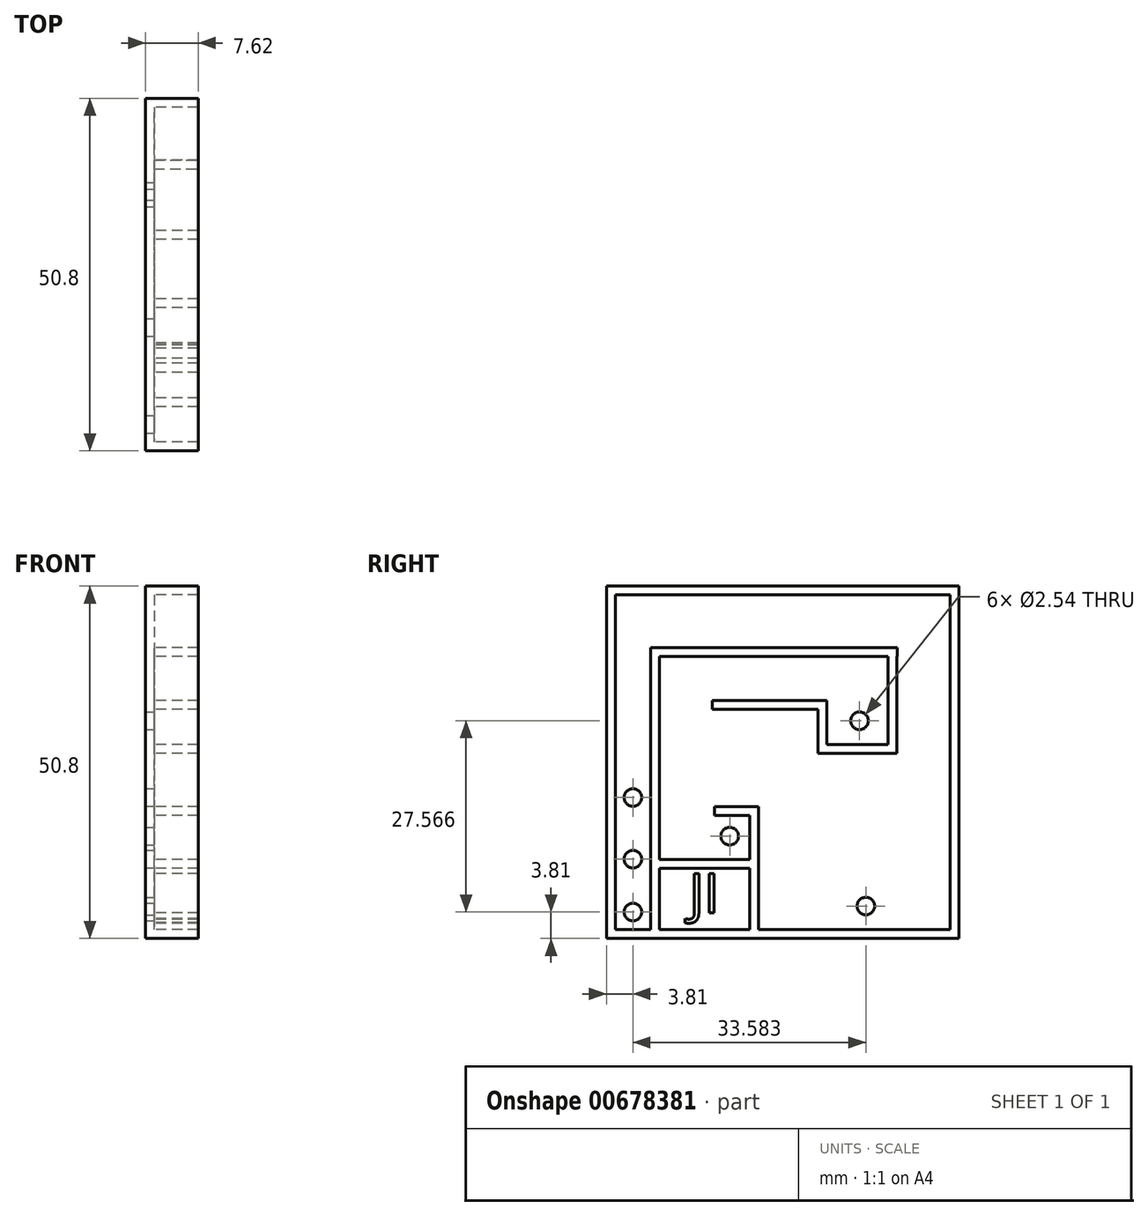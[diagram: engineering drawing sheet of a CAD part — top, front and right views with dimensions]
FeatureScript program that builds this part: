
annotation { "Feature Type Name" : "Feature", "Feature Type Description" : "" }
export const myFeature = defineFeature(function(context is Context, id is Id, definition is map)
    precondition{}
    {
        {
            var Q0;
            Q0=qCreatedBy(makeId("Right.planeOp"),FACE);
            var sketch = newSketch(context, id + "F0", { "sketchPlane" : qUnion([Q0])});
            skLineSegment(sketch, "E0", {"start": v(0, 0) * mm, "end": v(-50.8, 0) * mm});
            skLineSegment(sketch, "E1", {"start": v(-50.8, 0) * mm, "end": v(-50.8, 50.8) * mm});
            skLineSegment(sketch, "E2", {"start": v(-50.8, 50.8) * mm, "end": v(0, 50.8) * mm});
            skLineSegment(sketch, "E3", {"start": v(0, 50.8) * mm, "end": v(0, 0) * mm});
            skSolve(sketch);
        }
        {
            var Q0;
            Q0 = qSketchRegion(id + "F0", true);
            var Q1;
            Q1=makeQuery(id+"F0.imprint","IMPRINT",FACE,{"disambiguationData":[TD([[makeQuery(id+"F0.imprint","IMPRINT",EDGE,{"derivedFrom":sQuery(id+"F0.wireOp",EDGE,"E0")}),-1.0]])]});
            extrude(context, id + "F1", {"entities" : qUnion([Q0, Q1]), "depth" : 7.62 * mm, "offsetDistance" : 25.4 * mm});
        }
        {
            var Q0;
            Q0=makeQuery(id+"F1.opExtrude","CAP_FACE",FACE,{"disambiguationData":[OSD([sQuery(id+"F0.wireOp",EDGE,"E0"),sQuery(id+"F0.wireOp",EDGE,"E1"),sQuery(id+"F0.wireOp",EDGE,"E2"),sQuery(id+"F0.wireOp",EDGE,"E3")])],"isStart":false});
            shell(context, id + "F2", {"entities" : qUnion([Q0]), "thickness" : 1.27 * mm});
        }
        {
            var Q0;
            Q0=makeQuery(id+"F2.opShell","OFFSET_FACE",FACE,{"disambiguationData":[OSD([sQuery(id+"F0.wireOp",EDGE,"E0"),sQuery(id+"F0.wireOp",EDGE,"E1"),sQuery(id+"F0.wireOp",EDGE,"E2"),sQuery(id+"F0.wireOp",EDGE,"E3")])]});
            var sketch = newSketch(context, id + "F3", { "sketchPlane" : qUnion([Q0])});
            skLineSegment(sketch, "E4", {"start": v(-49.53, 1.27) * mm, "end": v(-44.45, 1.27) * mm});
            skLineSegment(sketch, "E5", {"start": v(-44.45, 1.27) * mm, "end": v(-44.45, 41.91) * mm});
            skLineSegment(sketch, "E6", {"start": v(-44.45, 41.91) * mm, "end": v(-43.18, 41.91) * mm});
            skLineSegment(sketch, "E7", {"start": v(-43.18, 41.91) * mm, "end": v(-43.18, 0) * mm});
            skSolve(sketch);
        }
        {
            var Q0;
            Q0 = qSketchRegion(id + "F3", true);
            var Q1;
            {var subQ0=sQuery(id+"F3.wireOp",EDGE,"E5");Q1=makeQuery(id+"F3.imprint","IMPRINT",FACE,{"disambiguationData":[TD([[makeQuery(id+"F3.imprint","IMPRINT",EDGE,{"derivedFrom":subQ0}),-1.0]])]});}
            extrude(context, id + "F4", {"entities" : qUnion([Q0, Q1]), "operationType" : NewBodyOperationType.ADD, "depth" : 6.35 * mm, "offsetDistance" : 25.4 * mm});
        }
        {
            var Q0;
            Q0=makeQuery(id+"F2.opShell","OFFSET_FACE",FACE,{"disambiguationData":[OSD([sQuery(id+"F0.wireOp",EDGE,"E0"),sQuery(id+"F0.wireOp",EDGE,"E1"),sQuery(id+"F0.wireOp",EDGE,"E2"),sQuery(id+"F0.wireOp",EDGE,"E3")])]});
            var sketch = newSketch(context, id + "F5", { "sketchPlane" : qUnion([Q0])});
            skCircle(sketch, "E8", {"center": v(-47, 3.81) * mm, "radius": 1.27 * mm});
            skCircle(sketch, "E9", {"center": v(-47, 11.43) * mm, "radius": 1.27 * mm});
            skCircle(sketch, "E10", {"center": v(-47, 20.32) * mm, "radius": 1.27 * mm});
            skSolve(sketch);
        }
        {
            var Q0;
            Q0=makeQuery(id+"F5.imprint","IMPRINT",FACE,{"disambiguationData":[TD([[makeQuery(id+"F5.imprint","IMPRINT",EDGE,{"derivedFrom":sQuery(id+"F5.wireOp",EDGE,"E8")}),1.0]])]});
            var Q1;
            Q1=makeQuery(id+"F5.imprint","IMPRINT",FACE,{"disambiguationData":[TD([[makeQuery(id+"F5.imprint","IMPRINT",EDGE,{"derivedFrom":sQuery(id+"F5.wireOp",EDGE,"E9")}),1.0]])]});
            extrude(context, id + "F6", {"entities" : qUnion([Q0, Q1]), "operationType" : NewBodyOperationType.REMOVE, "oppositeDirection" : true, "depth" : 2540 * mm, "offsetDistance" : 25.4 * mm});
        }
        {
            var Q0;
            Q0 = qSketchRegion(id + "F5", true);
            extrude(context, id + "F7", {"entities" : qUnion([Q0]), "operationType" : NewBodyOperationType.REMOVE, "oppositeDirection" : true, "depth" : 25.4 * mm, "offsetDistance" : 25.4 * mm});
        }
        {
            var Q0;
            Q0=makeQuery(id+"F2.opShell","OFFSET_FACE",FACE,{"disambiguationData":[OSD([sQuery(id+"F0.wireOp",EDGE,"E0"),sQuery(id+"F0.wireOp",EDGE,"E1"),sQuery(id+"F0.wireOp",EDGE,"E2"),sQuery(id+"F0.wireOp",EDGE,"E3")])]});
            var sketch = newSketch(context, id + "F8", { "sketchPlane" : qUnion([Q0])});
            skLineSegment(sketch, "E11", {"start": v(-43.18, 41.91) * mm, "end": v(-8.89, 41.91) * mm});
            skLineSegment(sketch, "E12", {"start": v(-8.89, 41.91) * mm, "end": v(-8.89, 40.64) * mm});
            skLineSegment(sketch, "E13", {"start": v(-8.89, 40.64) * mm, "end": v(-43.18, 40.64) * mm});
            skSolve(sketch);
        }
        {
            var Q0;
            Q0=makeQuery(id+"F8.imprint","IMPRINT",FACE,{"disambiguationData":[TD([[makeQuery(id+"F8.imprint","IMPRINT",EDGE,{"derivedFrom":sQuery(id+"F8.wireOp",EDGE,"E11")}),1.0]])]});
            var sketch = newSketch(context, id + "F9", { "sketchPlane" : qUnion([Q0])});
            skLineSegment(sketch, "E14", {"start": v(-8.9, 39.35) * mm, "end": v(-8.9, 26.65) * mm});
            skLineSegment(sketch, "E15", {"start": v(-8.9, 26.65) * mm, "end": v(-19.07, 26.65) * mm});
            skLineSegment(sketch, "E16", {"start": v(-19.07, 26.65) * mm, "end": v(-19.07, 27.92) * mm});
            skLineSegment(sketch, "E17", {"start": v(-19.07, 27.92) * mm, "end": v(-10.18, 27.92) * mm});
            skLineSegment(sketch, "E18", {"start": v(-10.18, 27.92) * mm, "end": v(-10.18, 40.88) * mm});
            skLineSegment(sketch, "E19", {"start": v(-8.9, 39.35) * mm, "end": v(-8.9, 40.64) * mm});
            skLineSegment(sketch, "E20", {"start": v(-8.9, 40.64) * mm, "end": v(-10.18, 40.88) * mm});
            skSolve(sketch);
        }
        {
            var Q0;
            Q0 = qSketchRegion(id + "F9", true);
            extrude(context, id + "F10", {"entities" : qUnion([Q0]), "operationType" : NewBodyOperationType.ADD, "depth" : 6.35 * mm, "offsetDistance" : 25.4 * mm});
        }
        {
            var Q0;
            {var subQ0=sQuery(id+"F8.wireOp",EDGE,"E11");Q0=makeQuery(id+"F8.imprint","IMPRINT",FACE,{"disambiguationData":[TD([[makeQuery(id+"F8.imprint","IMPRINT",EDGE,{"derivedFrom":subQ0}),-1.0]])]});}
            extrude(context, id + "F11", {"entities" : qUnion([Q0]), "operationType" : NewBodyOperationType.ADD, "depth" : 6.35 * mm, "offsetDistance" : 25.4 * mm});
        }
        {
            var Q0;
            Q0=makeQuery(id+"F2.opShell","OFFSET_FACE",FACE,{"disambiguationData":[OSD([sQuery(id+"F0.wireOp",EDGE,"E0"),sQuery(id+"F0.wireOp",EDGE,"E1"),sQuery(id+"F0.wireOp",EDGE,"E2"),sQuery(id+"F0.wireOp",EDGE,"E3")])]});
            var sketch = newSketch(context, id + "F12", { "sketchPlane" : qUnion([Q0])});
            skLineSegment(sketch, "E21", {"start": v(-19.07, 27.92) * mm, "end": v(-19.07, 34.27) * mm});
            skLineSegment(sketch, "E22", {"start": v(-19.07, 34.27) * mm, "end": v(-20.34, 34.27) * mm});
            skLineSegment(sketch, "E23", {"start": v(-20.34, 34.27) * mm, "end": v(-20.34, 26.65) * mm});
            skLineSegment(sketch, "E24", {"start": v(-20.34, 26.65) * mm, "end": v(-19.07, 26.65) * mm});
            skLineSegment(sketch, "E25", {"start": v(-20.34, 34.27) * mm, "end": v(-35.58, 34.27) * mm});
            skLineSegment(sketch, "E26", {"start": v(-35.58, 34.27) * mm, "end": v(-35.58, 33) * mm});
            skLineSegment(sketch, "E27", {"start": v(-35.58, 33) * mm, "end": v(-20.34, 33) * mm});
            skLineSegment(sketch, "E28", {"start": v(-20.34, 31.58) * mm, "end": v(-19.7, 31.58) * mm});
            skPoint(sketch, "E28.endSnap0", {"position": v(-19.7, 26.65) * mm});
            skLineSegment(sketch, "E29", {"start": v(-8.63, 19) * mm, "end": v(-8.63, 1.27) * mm});
            skLineSegment(sketch, "E30", {"start": v(-8.63, 1.27) * mm, "end": v(-8.63, 19) * mm});
            skLineSegment(sketch, "E31", {"start": v(-8.63, 19) * mm, "end": v(-9.9, 19) * mm});
            skLineSegment(sketch, "E32", {"start": v(-9.9, 19) * mm, "end": v(-9.9, 1.27) * mm});
            skLineSegment(sketch, "E33", {"start": v(-17.8, 19) * mm, "end": v(-17.8, 1.27) * mm});
            skLineSegment(sketch, "E34", {"start": v(-17.8, 1.27) * mm, "end": v(-17.8, 19) * mm});
            skLineSegment(sketch, "E35", {"start": v(-17.8, 19) * mm, "end": v(-19.07, 19) * mm});
            skLineSegment(sketch, "E36", {"start": v(-19.07, 19) * mm, "end": v(-19.07, 1.27) * mm});
            skLineSegment(sketch, "E37", {"start": v(-28.88, 1.27) * mm, "end": v(-28.88, 19) * mm});
            skLineSegment(sketch, "E38", {"start": v(-28.88, 19) * mm, "end": v(-30.15, 19) * mm});
            skLineSegment(sketch, "E39", {"start": v(-30.15, 19) * mm, "end": v(-30.15, 1.27) * mm});
            skLineSegment(sketch, "E40", {"start": v(-30.15, 19) * mm, "end": v(-35.23, 19) * mm});
            skLineSegment(sketch, "E41", {"start": v(-35.23, 19) * mm, "end": v(-35.23, 17.72) * mm});
            skLineSegment(sketch, "E42", {"start": v(-35.23, 17.72) * mm, "end": v(-30.15, 17.72) * mm});
            skLineSegment(sketch, "E43", {"start": v(-30.15, 17.72) * mm, "end": v(-30.15, 16.94) * mm});
            skLineSegment(sketch, "E44", {"start": v(-30.15, 16.94) * mm, "end": v(-30.15, 10.13) * mm});
            skLineSegment(sketch, "E45", {"start": v(-43.18, 10.13) * mm, "end": v(-30.15, 10.13) * mm});
            skLineSegment(sketch, "E46", {"start": v(-43.18, 11.4) * mm, "end": v(-30.15, 11.4) * mm});
            skLineSegment(sketch, "E47", {"start": v(-30.15, 11.4) * mm, "end": v(-30.15, 10.13) * mm});
            skLineSegment(sketch, "E48", {"start": v(-20.34, 33) * mm, "end": v(-19.07, 33) * mm});
            skSolve(sketch);
        }
        {
            var Q0;
            Q0 = qSketchRegion(id + "F12", true);
            var Q1;
            {var subQ6=sQuery(id+"F12.wireOp",EDGE,"E37");Q1=makeQuery(id+"F12.imprint","IMPRINT",FACE,{"disambiguationData":[TD([[makeQuery(id+"F12.imprint","IMPRINT",EDGE,{"derivedFrom":subQ6}),1.0]])]});}
            var Q2;
            {var subQ0=sQuery(id+"F12.wireOp",EDGE,"E45");Q2=makeQuery(id+"F12.imprint","IMPRINT",FACE,{"disambiguationData":[TD([[makeQuery(id+"F12.imprint","IMPRINT",EDGE,{"derivedFrom":subQ0}),1.0]])]});}
            var Q3;
            {var subQ0=sQuery(id+"F12.wireOp",EDGE,"E34");Q3=makeQuery(id+"F12.imprint","IMPRINT",FACE,{"disambiguationData":[TD([[makeQuery(id+"F12.imprint","IMPRINT",EDGE,{"derivedFrom":subQ0}),1.0]])]});}
            var Q4;
            {var subQ0=sQuery(id+"F12.wireOp",EDGE,"E30");Q4=makeQuery(id+"F12.imprint","IMPRINT",FACE,{"disambiguationData":[TD([[makeQuery(id+"F12.imprint","IMPRINT",EDGE,{"derivedFrom":subQ0}),1.0]])]});}
            var Q5;
            {var subQ0=sQuery(id+"F12.wireOp",EDGE,"E24");Q5=makeQuery(id+"F12.imprint","IMPRINT",FACE,{"disambiguationData":[TD([[makeQuery(id+"F12.imprint","IMPRINT",EDGE,{"derivedFrom":subQ0}),1.0]])]});}
            extrude(context, id + "F13", {"entities" : qUnion([Q0, Q1, Q2, Q3, Q4, Q5]), "operationType" : NewBodyOperationType.ADD, "depth" : 6.35 * mm, "offsetDistance" : 25.4 * mm});
        }
        {
            var Q0;
            {var subQ0=sQuery(id+"F0.wireOp",EDGE,"E0");Q0=makeQuery(id+"F13.boolean.opBoolean","SPLIT",FACE,{"disambiguationData":[TD([makeQuery(id+"F13.opExtrude","SWEPT_FACE",FACE,{"disambiguationData":[OSD([sQuery(id+"F12.wireOp",EDGE,"E39")])]})])],"derivedFrom":makeQuery(id+"F2.opShell","OFFSET_FACE",FACE,{"disambiguationData":[OSD([subQ0,sQuery(id+"F0.wireOp",EDGE,"E1"),sQuery(id+"F0.wireOp",EDGE,"E2"),sQuery(id+"F0.wireOp",EDGE,"E3")])]})});}
            var sketch = newSketch(context, id + "F14", { "sketchPlane" : qUnion([Q0])});
            skText(sketch, "E49", { "text": "JI", "fontName": "OpenSans-Regular.ttf"});
            const initialGuessF14  = {"E49": [-0.03887, 0.00367, 1, 0, 0.00572]};
            skSetInitialGuess(sketch, initialGuessF14);
            skSolve(sketch);
        }
        {
            var Q0;
            Q0 = qSketchRegion(id + "F14", true);
            extrude(context, id + "F15", {"entities" : qUnion([Q0]), "operationType" : NewBodyOperationType.ADD, "depth" : 6.35 * mm, "offsetDistance" : 25.4 * mm});
        }
        {
            var Q0;
            {var subQ0=sQuery(id+"F0.wireOp",EDGE,"E3");var subQ1=sQuery(id+"F0.wireOp",EDGE,"E1");var subQ2=sQuery(id+"F0.wireOp",EDGE,"E0");var subQ3=sQuery(id+"F0.wireOp",EDGE,"E2");Q0=makeQuery(id+"F13.boolean.opBoolean","SPLIT",FACE,{"disambiguationData":[TD([makeQuery(id+"F2.opShell","OFFSET_FACE",FACE,{"disambiguationData":[OSD([subQ1])]})])],"derivedFrom":makeQuery(id+"F2.opShell","OFFSET_FACE",FACE,{"disambiguationData":[OSD([subQ2,subQ1,subQ3,subQ0])]})});}
            var sketch = newSketch(context, id + "F16", { "sketchPlane" : qUnion([Q0])});
            skCircle(sketch, "E50", {"center": v(-14.32, 31.38) * mm, "radius": 1.27 * mm});
            skCircle(sketch, "E51", {"center": v(-33.04, 14.74) * mm, "radius": 1.27 * mm});
            skCircle(sketch, "E52", {"center": v(-13.4, 4.66) * mm, "radius": 1.27 * mm});
            skSolve(sketch);
        }
        {
            var Q0;
            Q0=makeQuery(id+"F16.imprint","IMPRINT",FACE,{"disambiguationData":[TD([[makeQuery(id+"F16.imprint","IMPRINT",EDGE,{"derivedFrom":sQuery(id+"F16.wireOp",EDGE,"E50")}),1.0]])]});
            var Q1;
            Q1=makeQuery(id+"F16.imprint","IMPRINT",FACE,{"disambiguationData":[TD([[makeQuery(id+"F16.imprint","IMPRINT",EDGE,{"derivedFrom":sQuery(id+"F16.wireOp",EDGE,"E51")}),1.0]])]});
            var Q2;
            Q2=makeQuery(id+"F16.imprint","IMPRINT",FACE,{"disambiguationData":[TD([[makeQuery(id+"F16.imprint","IMPRINT",EDGE,{"derivedFrom":sQuery(id+"F16.wireOp",EDGE,"E52")}),1.0]])]});
            extrude(context, id + "F17", {"entities" : qUnion([Q0, Q1, Q2]), "operationType" : NewBodyOperationType.REMOVE, "oppositeDirection" : true, "depth" : 254 * mm, "offsetDistance" : 25.4 * mm});
        }
    });
